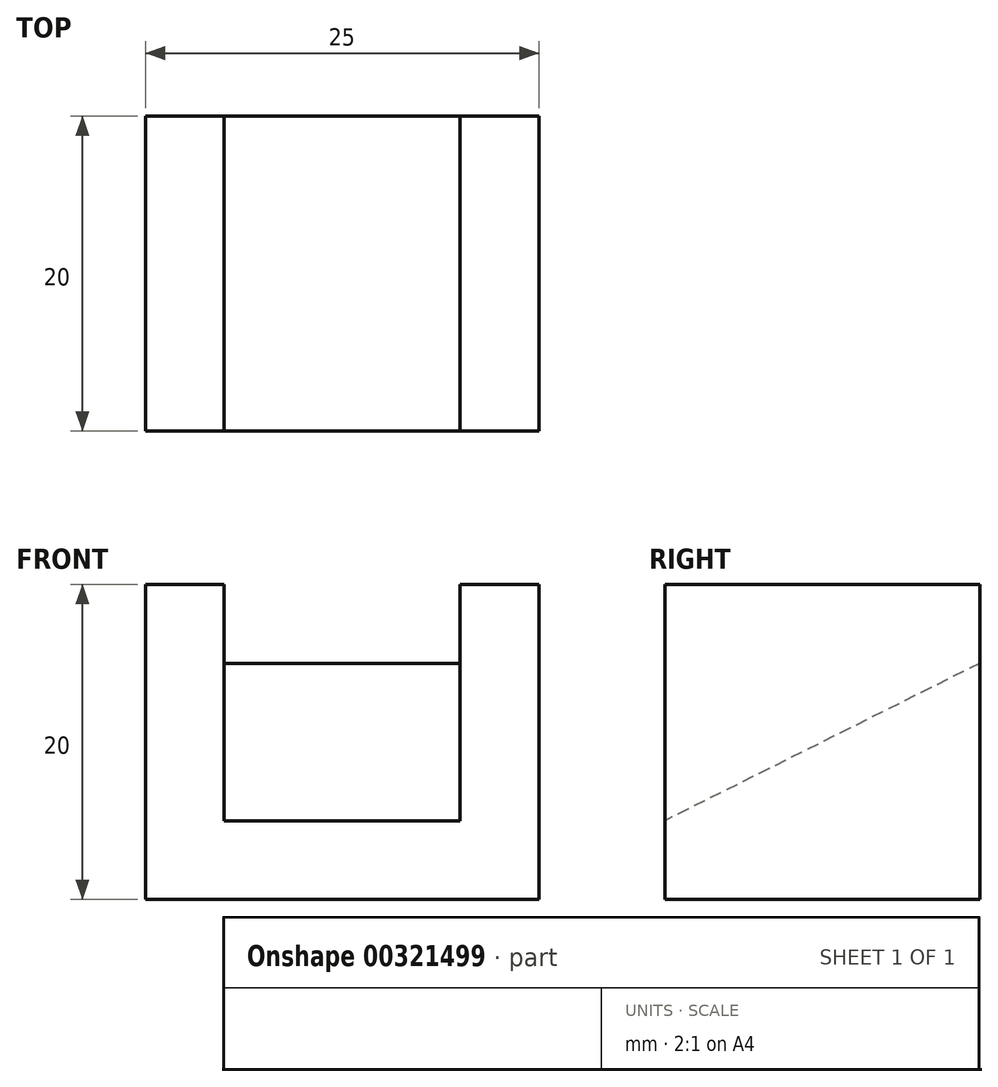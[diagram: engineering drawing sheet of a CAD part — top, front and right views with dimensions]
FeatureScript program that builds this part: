
annotation { "Feature Type Name" : "Feature", "Feature Type Description" : "" }
export const myFeature = defineFeature(function(context is Context, id is Id, definition is map)
    precondition{}
    {
        {
            var Q0;
            Q0=qCreatedBy(makeId("Front.planeOp"),FACE);
            var sketch = newSketch(context, id + "F0", { "sketchPlane" : qUnion([Q0])});
            skLineSegment(sketch, "E0", {"start": v(0, 0) * mm, "end": v(15, 0) * mm});
            skLineSegment(sketch, "E1", {"start": v(15, 0) * mm, "end": v(15, 15) * mm});
            skLineSegment(sketch, "E2", {"start": v(15, 15) * mm, "end": v(0, 15) * mm});
            skLineSegment(sketch, "E3", {"start": v(0, 15) * mm, "end": v(0, 0) * mm});
            skSolve(sketch);
        }
        {
            var Q0;
            Q0 = qSketchRegion(id + "F0", true);
            extrude(context, id + "F1", {"entities" : qUnion([Q0]), "endBound" : BoundingType.SYMMETRIC, "depth" : 20 * mm});
        }
        {
            var Q0;
            Q0=makeQuery(id+"F1.opExtrude","SWEPT_FACE",FACE,{"disambiguationData":[OSD([sQuery(id+"F0.wireOp",EDGE,"E3")])]});
            var sketch = newSketch(context, id + "F2", { "sketchPlane" : qUnion([Q0])});
            skLineSegment(sketch, "E4", {"start": v(-10, 15) * mm, "end": v(-10, 0) * mm});
            skLineSegment(sketch, "E5", {"start": v(-10, 0) * mm, "end": v(10, 0) * mm});
            skLineSegment(sketch, "E6", {"start": v(10, 0) * mm, "end": v(10, 5) * mm});
            skLineSegment(sketch, "E7", {"start": v(-10, 15) * mm, "end": v(10, 5) * mm});
            skSolve(sketch);
        }
        {
            var Q0;
            {var subQ0=sQuery(id+"F2.wireOp",EDGE,"E7");Q0=makeQuery(id+"F2.imprint","IMPRINT",FACE,{"disambiguationData":[TD([[makeQuery(id+"F2.imprint","IMPRINT",EDGE,{"derivedFrom":subQ0}),1.0]])]});}
            extrude(context, id + "F3", {"entities" : qUnion([Q0]), "operationType" : NewBodyOperationType.REMOVE, "endBound" : BoundingType.THROUGH_ALL, "oppositeDirection" : true, "depth" : 25 * mm});
        }
        {
            var Q0;
            Q0=makeQuery(id+"F1.opExtrude","SWEPT_FACE",FACE,{"disambiguationData":[OSD([sQuery(id+"F0.wireOp",EDGE,"E3")])]});
            var sketch = newSketch(context, id + "F4", { "sketchPlane" : qUnion([Q0])});
            skLineSegment(sketch, "E8", {"start": v(-10, 0) * mm, "end": v(-10, 20) * mm});
            skLineSegment(sketch, "E9", {"start": v(-10, 20) * mm, "end": v(10, 20) * mm});
            skLineSegment(sketch, "E10", {"start": v(10, 20) * mm, "end": v(10, 0) * mm});
            skLineSegment(sketch, "E11", {"start": v(10, 0) * mm, "end": v(-10, 0) * mm});
            skSolve(sketch);
        }
        {
            var Q0;
            Q0 = qSketchRegion(id + "F4", true);
            extrude(context, id + "F5", {"entities" : qUnion([Q0]), "operationType" : NewBodyOperationType.ADD, "depth" : 5 * mm});
        }
        {
            var Q0;
            Q0=makeQuery(id+"F1.opExtrude","SWEPT_FACE",FACE,{"disambiguationData":[OSD([sQuery(id+"F0.wireOp",EDGE,"E1")])]});
            var sketch = newSketch(context, id + "F6", { "sketchPlane" : qUnion([Q0])});
            skLineSegment(sketch, "E12", {"start": v(-10, 0) * mm, "end": v(-10, 20) * mm});
            skLineSegment(sketch, "E13", {"start": v(-10, 20) * mm, "end": v(10, 20) * mm});
            skLineSegment(sketch, "E14", {"start": v(10, 20) * mm, "end": v(10, 0) * mm});
            skLineSegment(sketch, "E15", {"start": v(10, 0) * mm, "end": v(-10, 0) * mm});
            skSolve(sketch);
        }
        {
            var Q0;
            Q0 = qSketchRegion(id + "F6", true);
            extrude(context, id + "F7", {"entities" : qUnion([Q0]), "operationType" : NewBodyOperationType.ADD, "depth" : 5 * mm});
        }
    });
